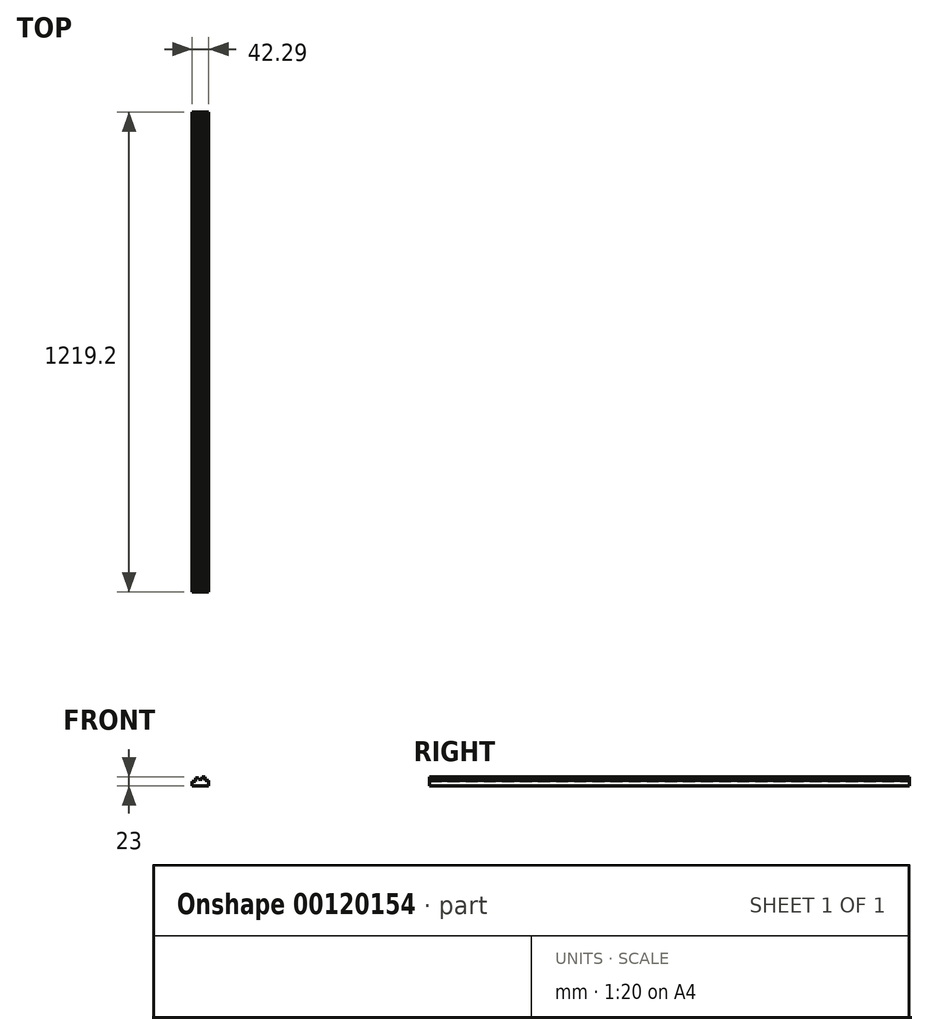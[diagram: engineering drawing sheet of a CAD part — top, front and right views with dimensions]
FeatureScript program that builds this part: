
annotation { "Feature Type Name" : "Feature", "Feature Type Description" : "" }
export const myFeature = defineFeature(function(context is Context, id is Id, definition is map)
    precondition{}
    {
        {
            var Q0;
            Q0=qCreatedBy(makeId("Front.planeOp"),FACE);
            var sketch = newSketch(context, id + "F0", { "sketchPlane" : qUnion([Q0])});
            skLineSegment(sketch, "E0", {"start": v(0, 0) * mm, "end": v(0, 11) * mm});
            skLineSegment(sketch, "E1", {"start": v(0, 11) * mm, "end": v(8.46, 11) * mm});
            skLineSegment(sketch, "E2", {"start": v(8.46, 11) * mm, "end": v(8.46, 20) * mm});
            skLineSegment(sketch, "E3", {"start": v(8.46, 20) * mm, "end": v(16.92, 20) * mm});
            skLineSegment(sketch, "E4", {"start": v(16.92, 20) * mm, "end": v(16.92, 17) * mm});
            skLineSegment(sketch, "E5", {"start": v(16.92, 17) * mm, "end": v(25.37, 17) * mm});
            skLineSegment(sketch, "E6", {"start": v(0, 0) * mm, "end": v(42.3, 0) * mm});
            skLineSegment(sketch, "E7", {"start": v(42.3, 0) * mm, "end": v(42.3, 14) * mm});
            skLineSegment(sketch, "E8", {"start": v(42.3, 14) * mm, "end": v(33.83, 14) * mm});
            skLineSegment(sketch, "E9", {"start": v(33.83, 14) * mm, "end": v(33.83, 23) * mm});
            skLineSegment(sketch, "E10", {"start": v(33.83, 23) * mm, "end": v(25.37, 23) * mm});
            skLineSegment(sketch, "E11", {"start": v(25.37, 23) * mm, "end": v(25.37, 17) * mm});
            skSolve(sketch);
        }
        {
            var Q0;
            Q0=makeQuery(id+"F0.imprint","IMPRINT",FACE,{"disambiguationData":[TD([[makeQuery(id+"F0.imprint","IMPRINT",EDGE,{"derivedFrom":sQuery(id+"F0.wireOp",EDGE,"E0")}),-1.0]])]});
            extrude(context, id + "F1", {"entities" : qUnion([Q0]), "depth" : 1219.2 * mm});
        }
    });
